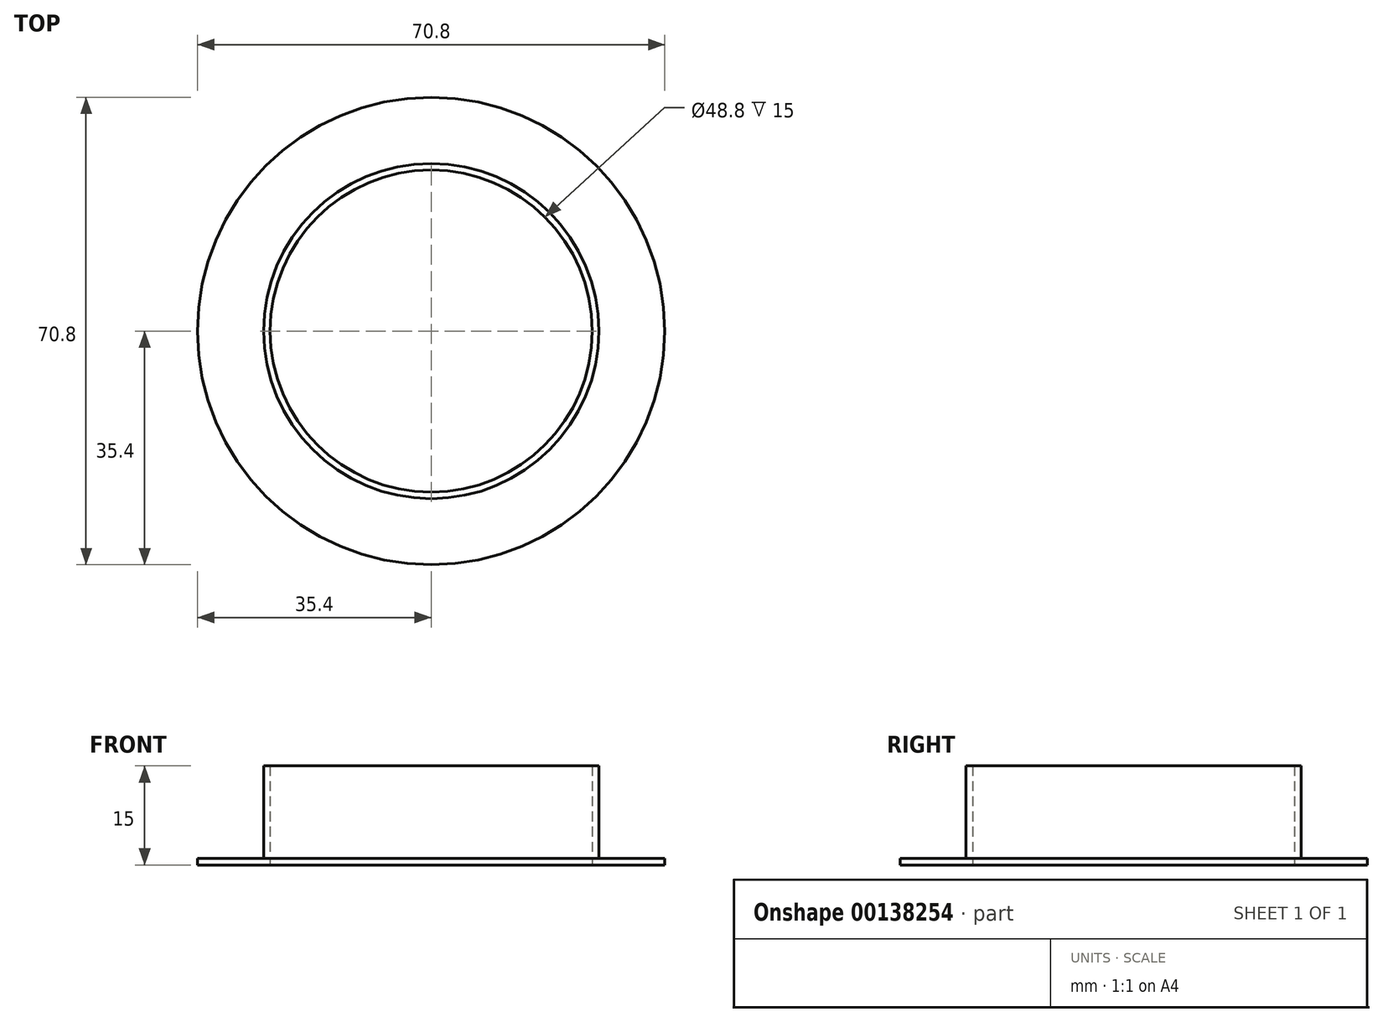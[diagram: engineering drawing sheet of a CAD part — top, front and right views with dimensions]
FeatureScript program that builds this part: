
annotation { "Feature Type Name" : "Feature", "Feature Type Description" : "" }
export const myFeature = defineFeature(function(context is Context, id is Id, definition is map)
    precondition{}
    {
        {
            var Q0;
            Q0=qCreatedBy(makeId("Top.planeOp"),FACE);
            var sketch = newSketch(context, id + "F0", { "sketchPlane" : qUnion([Q0])});
            skCircle(sketch, "E0", {"center": v(0, 0) * mm, "radius": 25.4 * mm});
            skCircle(sketch, "E1", {"center": v(0, 0) * mm, "radius": 24.4 * mm});
            skSolve(sketch);
        }
        {
            var Q0;
            Q0 = qSketchRegion(id + "F0", true);
            extrude(context, id + "F1", {"entities" : qUnion([Q0]), "depth" : 15 * mm});
        }
        {
            var Q0;
            Q0=qCreatedBy(makeId("Top.planeOp"),FACE);
            var sketch = newSketch(context, id + "F2", { "sketchPlane" : qUnion([Q0])});
            skCircle(sketch, "E2", {"center": v(0, 0) * mm, "radius": 35.4 * mm});
            skCircle(sketch, "E3.0", {"center": v(0, 0) * mm, "radius": 25.4 * mm});
            skSolve(sketch);
        }
        {
            var Q0;
            Q0 = qSketchRegion(id + "F2", true);
            extrude(context, id + "F3", {"entities" : qUnion([Q0]), "operationType" : NewBodyOperationType.ADD, "depth" : 1 * mm});
        }
    });
